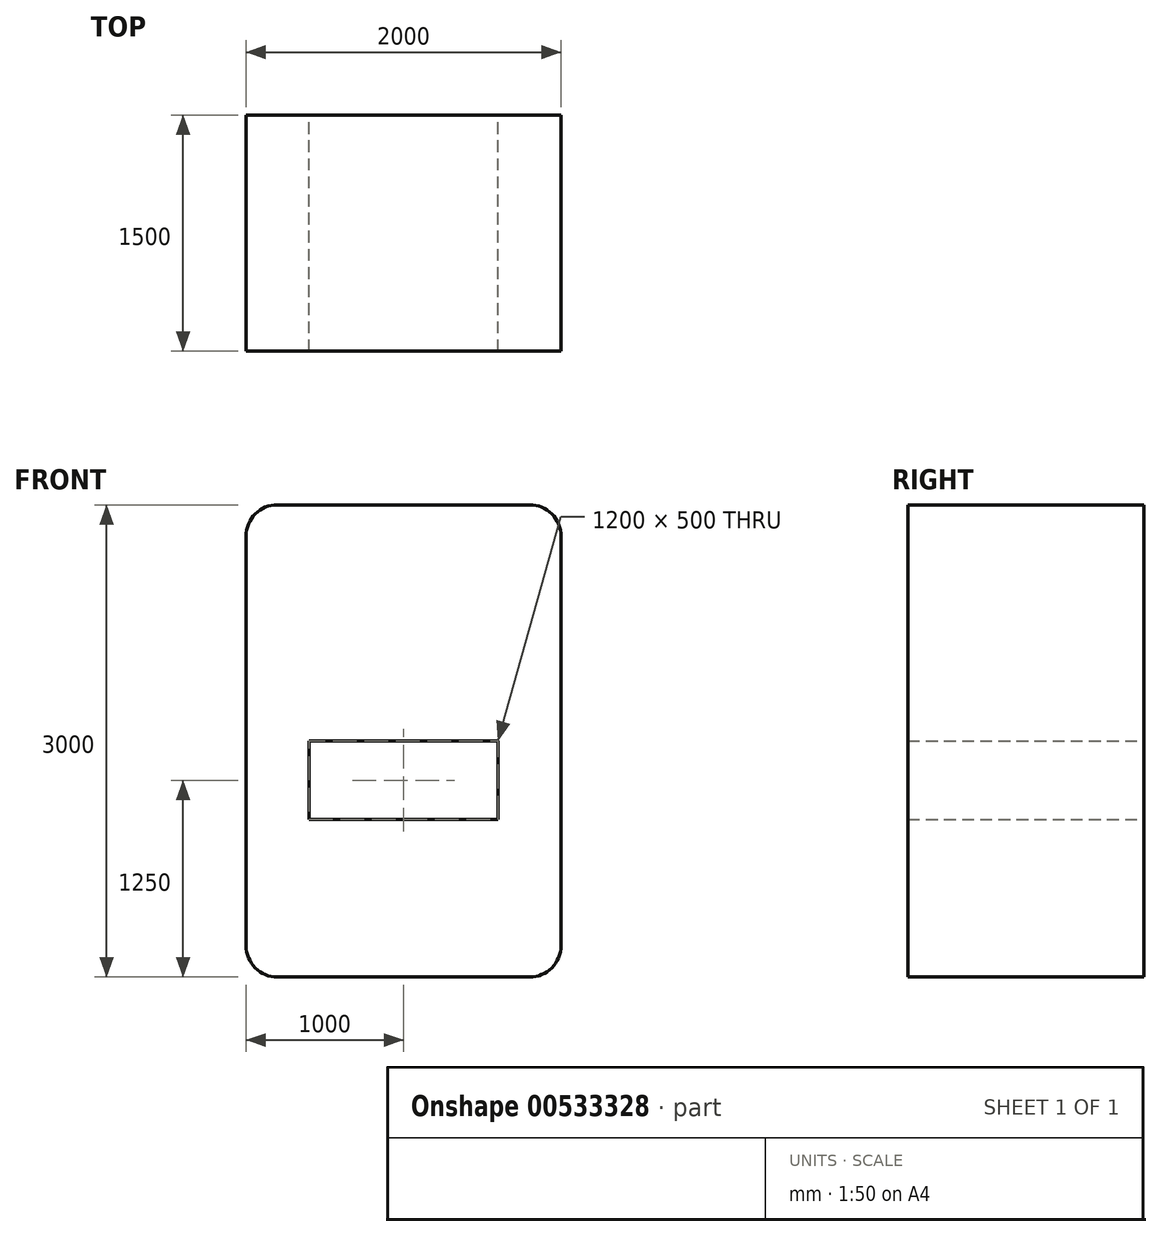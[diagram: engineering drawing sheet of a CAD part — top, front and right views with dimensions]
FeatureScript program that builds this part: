
annotation { "Feature Type Name" : "Feature", "Feature Type Description" : "" }
export const myFeature = defineFeature(function(context is Context, id is Id, definition is map)
    precondition{}
    {
        {
            var Q0;
            Q0=qCreatedBy(makeId("Front.planeOp"),FACE);
            var sketch = newSketch(context, id + "F0", { "sketchPlane" : qUnion([Q0])});
            skLineSegment(sketch, "E0.bottom", {"start": v(-800, 0) * mm, "end": v(800, 0) * mm});
            skLineSegment(sketch, "E0.top", {"start": v(-800, -3000) * mm, "end": v(800, -3000) * mm});
            skLineSegment(sketch, "E0.left", {"start": v(-1000, -200) * mm, "end": v(-1000, -2800) * mm});
            skLineSegment(sketch, "E0.right", {"start": v(1000, -200) * mm, "end": v(1000, -2800) * mm});
            skLineSegment(sketch, "E1.bottom", {"start": v(-600, -1500) * mm, "end": v(600, -1500) * mm});
            skLineSegment(sketch, "E1.top", {"start": v(-600, -2000) * mm, "end": v(600, -2000) * mm});
            skLineSegment(sketch, "E1.left", {"start": v(-600, -1500) * mm, "end": v(-600, -2000) * mm});
            skLineSegment(sketch, "E1.right", {"start": v(600, -1500) * mm, "end": v(600, -2000) * mm});
            skPoint(sketch, "E2.visualSharp", {"position": v(-1000, 0) * mm});
            skArc(sketch, "E2.filletArc", {"start": v(-800, 0) * mm, "mid": v(-941.42, -58.58) * mm, "end": v(-1000, -200) * mm});
            skPoint(sketch, "E3.visualSharp", {"position": v(1000, 0) * mm});
            skArc(sketch, "E3.filletArc", {"start": v(1000, -200) * mm, "mid": v(941.42, -58.58) * mm, "end": v(800, 0) * mm});
            skPoint(sketch, "E4.visualSharp", {"position": v(-1000, -3000) * mm});
            skArc(sketch, "E4.filletArc", {"start": v(-1000, -2800) * mm, "mid": v(-941.42, -2941.42) * mm, "end": v(-800, -3000) * mm});
            skPoint(sketch, "E5.visualSharp", {"position": v(1000, -3000) * mm});
            skArc(sketch, "E5.filletArc", {"start": v(800, -3000) * mm, "mid": v(941.42, -2941.42) * mm, "end": v(1000, -2800) * mm});
            skSolve(sketch);
        }
        {
            var Q0;
            Q0=makeQuery(id+"F0.imprint","IMPRINT",FACE,{"disambiguationData":[TD([[makeQuery(id+"F0.imprint","IMPRINT",EDGE,{"derivedFrom":sQuery(id+"F0.wireOp",EDGE,"E0.bottom")}),-1.0]])]});
            extrude(context, id + "F1", {"entities" : qUnion([Q0]), "depth" : 1500 * mm, "offsetDistance" : 25 * mm});
        }
    });
